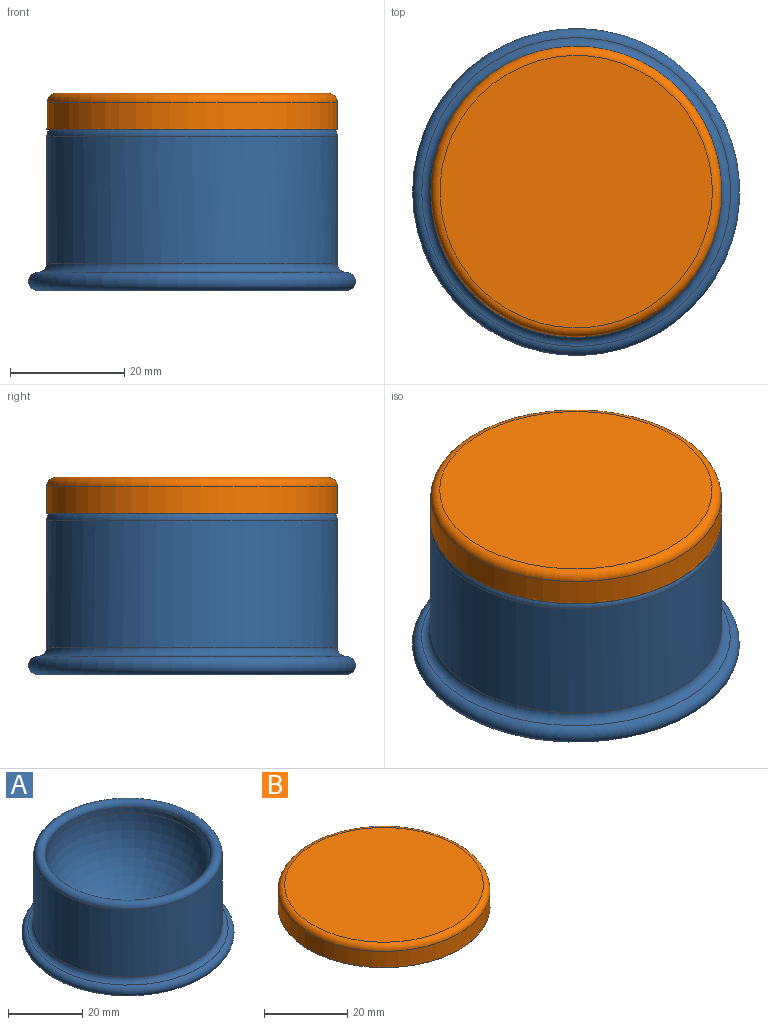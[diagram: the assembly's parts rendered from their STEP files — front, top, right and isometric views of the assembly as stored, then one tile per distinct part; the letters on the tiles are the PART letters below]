
ASSEMBLY  parts=2 mates=1
PART A: 8 faces, bbox 61.9x61.9x28.6 mm
  f0: cylinder r=22.23mm len=44.45mm, axis (0,0,-1), area 239.4mm2, adj f6,f7
  f1: cylinder r=25.4mm len=50.8mm, axis (0,0,-1), area 3547mm2, adj f5,f6
  f2: plane 53.98x53.98mm, normal (0,0,-1), area 2288.1mm2, adj f4
  f3: plane 0.25x0.25mm, normal (0,0,1), area 0.1mm2, adj f7
  f4: torus R=26.99mm, axis (0,0,-1), area 877.3mm2, adj f2,f5
  f5: torus R=26.99mm, axis (0,0,-1), area 407mm2, adj f1,f4
  f6: torus R=23.81mm, axis (0,0,1), area 746.2mm2, adj f0,f1
  f7: torus R=0.13mm, axis (0,0,-1), area 3095.9mm2, adj f0,f3
PART B: 8 faces, bbox 55x55x7.5 mm
  f0: cylinder r=25.4mm len=50.8mm, axis (0,0,-1), area 760.1mm2, adj f2,f3
  f1: plane 47.63x47.63mm, normal (0,0,1), area 1781.4mm2, adj f3
  f2: plane 50.8x50.8mm, normal (0,0,-1), area 0.1mm2, adj f0,f4
  f3: torus R=23.81mm, axis (0,0,1), area 388.9mm2, adj f0,f1
  f4: torus R=23.81mm, axis (0,0,-1), area 731.1mm2, adj f2,f7
  f5: plane 41.28x41.28mm, normal (0,0,-1), area 1338mm2, adj f6
  f6: torus R=20.64mm, axis (0,0,1), area 339.2mm2, adj f5,f7
  f7: cylinder r=22.23mm len=44.45mm, axis (0,0,1), area 204.4mm2, adj f4,f6
PLACE A t=(-8.67,7.1,4.63)mm
PLACE B t=(-8.67,7.1,20.05)mm
MATE slider B.f0 <-> A.f1  axis (0,0,-1) through (-8.67,7.1,16.88)mm
